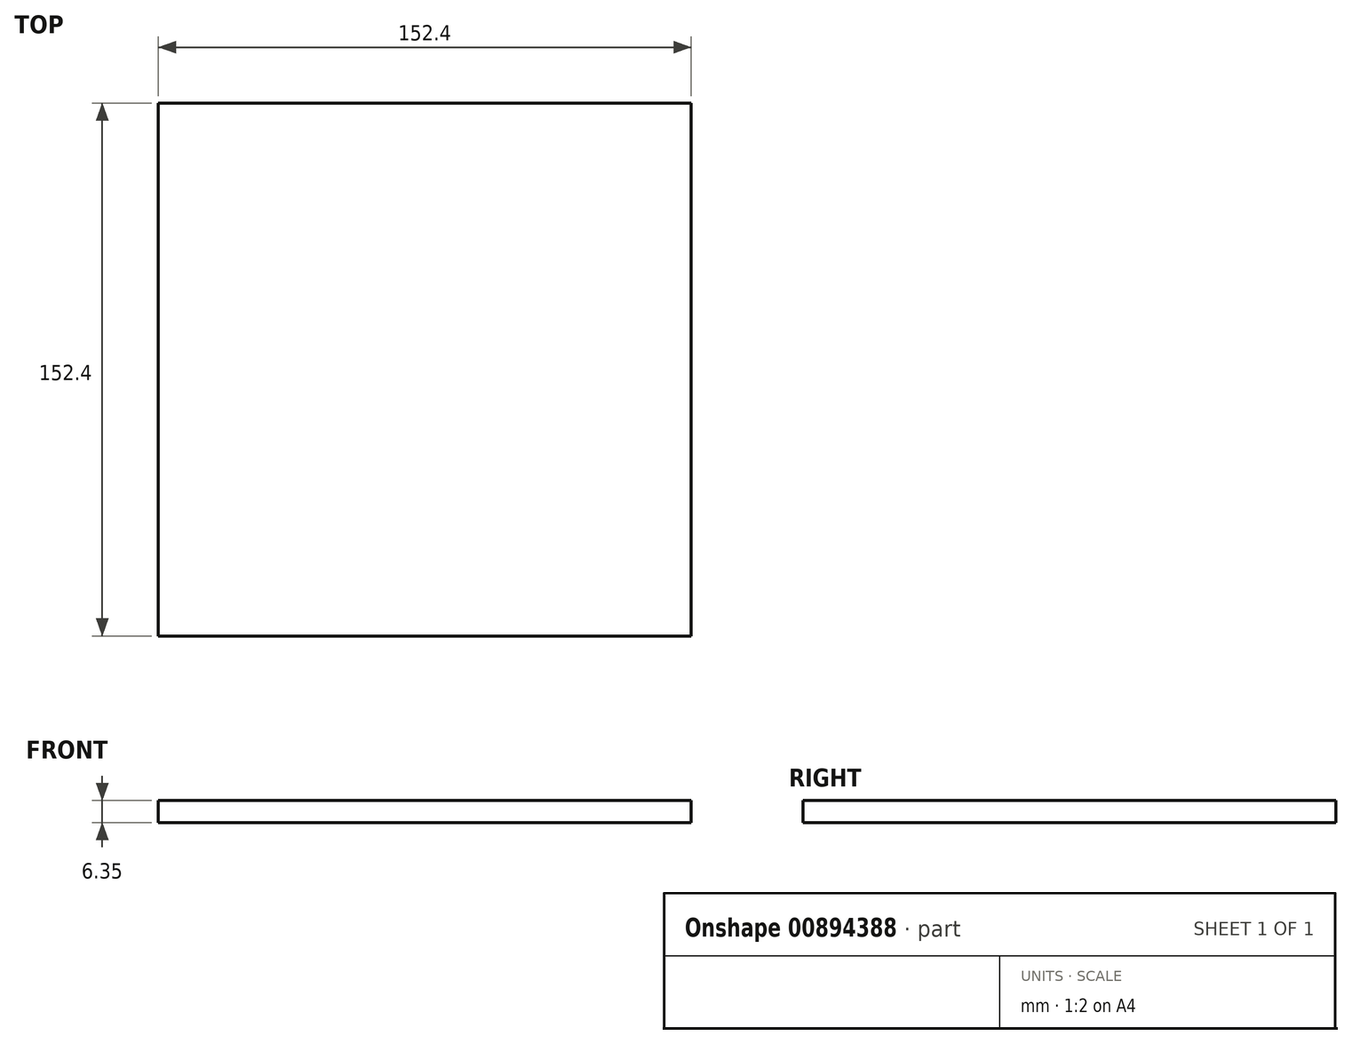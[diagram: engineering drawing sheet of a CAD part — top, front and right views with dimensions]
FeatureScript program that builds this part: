
annotation { "Feature Type Name" : "Feature", "Feature Type Description" : "" }
export const myFeature = defineFeature(function(context is Context, id is Id, definition is map)
    precondition{}
    {
        {
            var Q0;
            Q0=qCreatedBy(makeId("Top.planeOp"), FACE);
            var sketch = newSketch(context, id + "F0", { "sketchPlane" : qUnion([Q0])});
            skLineSegment(sketch, "E0.bottom", {"start": v(-76.2, 76.2) * mm, "end": v(76.2, 76.2) * mm});
            skLineSegment(sketch, "E0.top", {"start": v(-76.2, -76.2) * mm, "end": v(76.2, -76.2) * mm});
            skLineSegment(sketch, "E0.left", {"start": v(-76.2, 76.2) * mm, "end": v(-76.2, -76.2) * mm});
            skLineSegment(sketch, "E0.right", {"start": v(76.2, 76.2) * mm, "end": v(76.2, -76.2) * mm});
            skPoint(sketch, "E0.middle", {"position": v(0, 0) * mm});
            skSolve(sketch);
        }
        {
            var Q0;
            Q0 = qSketchRegion(id + "F0", true);
            extrude(context, id + "F1", {"entities" : qUnion([Q0]), "depth" : 6.35 * mm, "offsetDistance" : 25.4 * mm});
        }
    });
